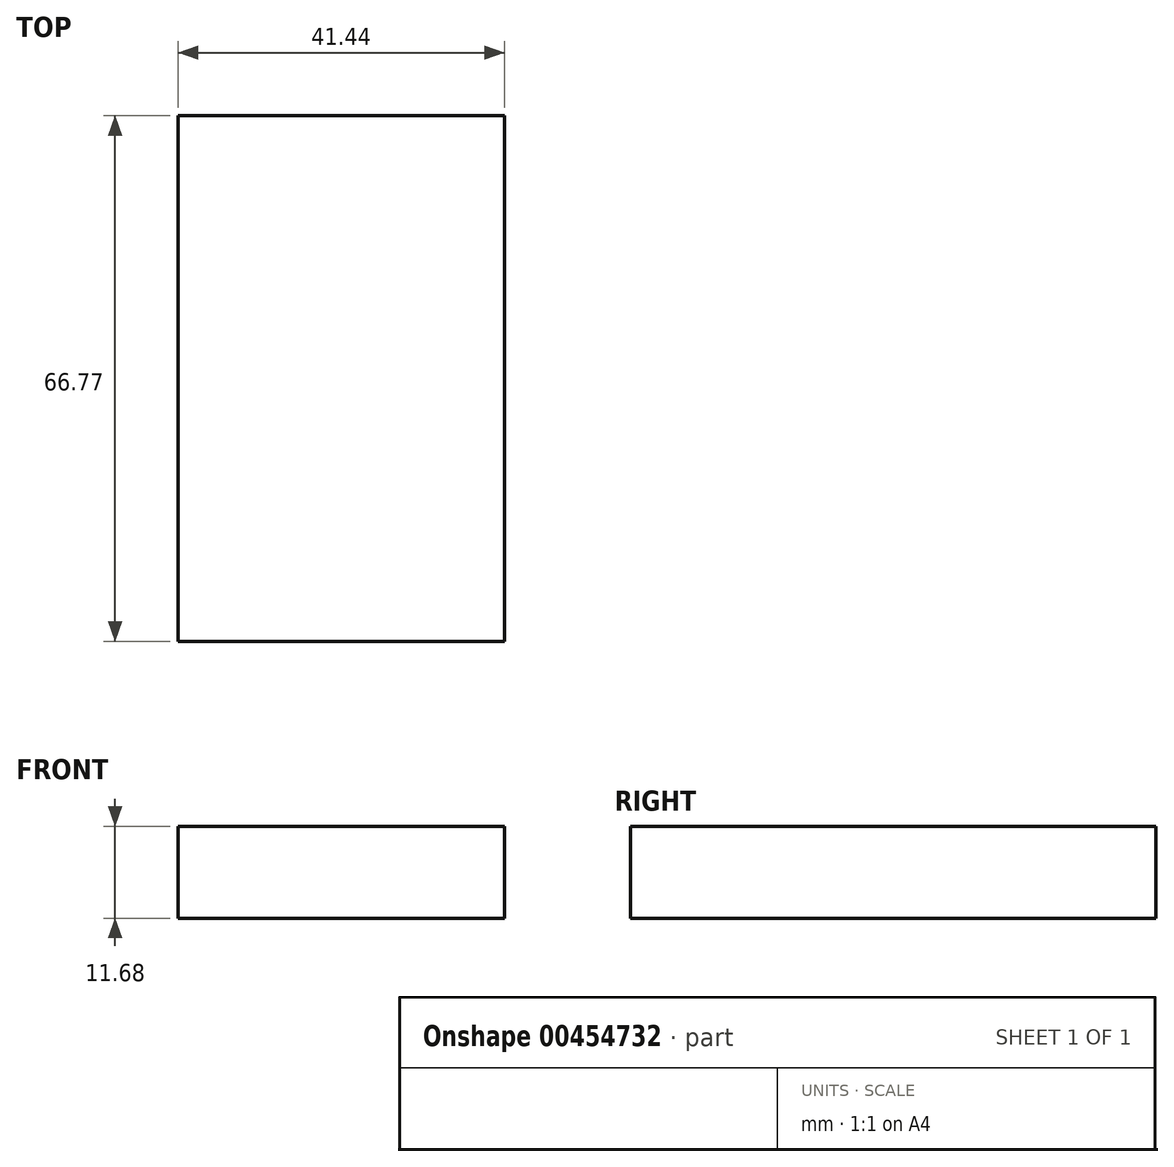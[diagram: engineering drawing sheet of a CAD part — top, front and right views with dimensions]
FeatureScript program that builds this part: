
annotation { "Feature Type Name" : "Feature", "Feature Type Description" : "" }
export const myFeature = defineFeature(function(context is Context, id is Id, definition is map)
    precondition{}
    {
        {
            var Q0;
            Q0=qCreatedBy(makeId("Top.planeOp"),FACE);
            var sketch = newSketch(context, id + "F0", { "sketchPlane" : qUnion([Q0])});
            skLineSegment(sketch, "E0.bottom", {"start": v(0, 0) * mm, "end": v(41.44, 0) * mm});
            skLineSegment(sketch, "E0.top", {"start": v(0, -66.77) * mm, "end": v(41.44, -66.77) * mm});
            skLineSegment(sketch, "E0.left", {"start": v(0, 0) * mm, "end": v(0, -66.77) * mm});
            skLineSegment(sketch, "E0.right", {"start": v(41.44, 0) * mm, "end": v(41.44, -66.77) * mm});
            skSolve(sketch);
        }
        {
            var Q0;
            Q0=makeQuery(id+"F0.imprint","IMPRINT",FACE,{"disambiguationData":[TD([[makeQuery(id+"F0.imprint","IMPRINT",EDGE,{"derivedFrom":sQuery(id+"F0.wireOp",EDGE,"E0.bottom")}),-1.0]])]});
            extrude(context, id + "F1", {"entities" : qUnion([Q0]), "depth" : 11.68 * mm});
        }
    });
